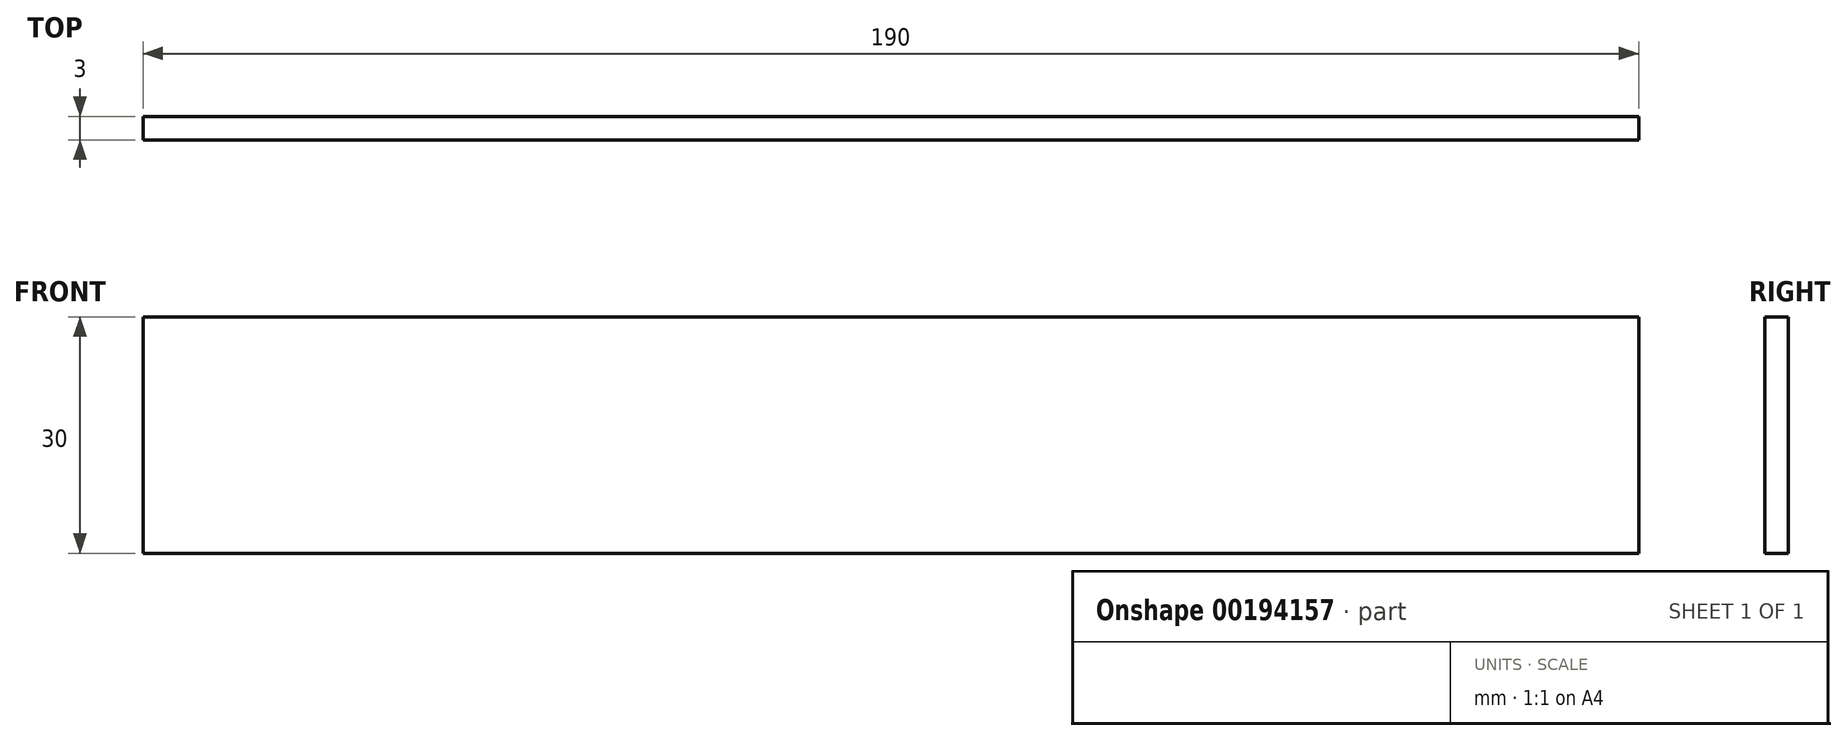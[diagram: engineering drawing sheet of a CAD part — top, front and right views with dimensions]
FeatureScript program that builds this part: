
annotation { "Feature Type Name" : "Feature", "Feature Type Description" : "" }
export const myFeature = defineFeature(function(context is Context, id is Id, definition is map)
    precondition{}
    {
        {
            var Q0;
            Q0=qCreatedBy(makeId("Front.planeOp"),FACE);
            var sketch = newSketch(context, id + "F0", { "sketchPlane" : qUnion([Q0])});
            skLineSegment(sketch, "E0.bottom", {"start": v(-95, 15) * mm, "end": v(95, 15) * mm});
            skLineSegment(sketch, "E0.top", {"start": v(-95, -15) * mm, "end": v(95, -15) * mm});
            skLineSegment(sketch, "E0.left", {"start": v(-95, 15) * mm, "end": v(-95, -15) * mm});
            skLineSegment(sketch, "E0.right", {"start": v(95, 15) * mm, "end": v(95, -15) * mm});
            skPoint(sketch, "E0.middle", {"position": v(0, 0) * mm});
            skLineSegment(sketch, "E1", {"start": v(-95, -1.75) * mm, "end": v(95, -1.75) * mm});
            skLineSegment(sketch, "E2", {"start": v(-95, 1.75) * mm, "end": v(95, 1.75) * mm});
            skSolve(sketch);
        }
        {
            var Q0;
            Q0 = qSketchRegion(id + "F0", true);
            extrude(context, id + "F1", {"entities" : qUnion([Q0]), "depth" : 3 * mm});
        }
    });
